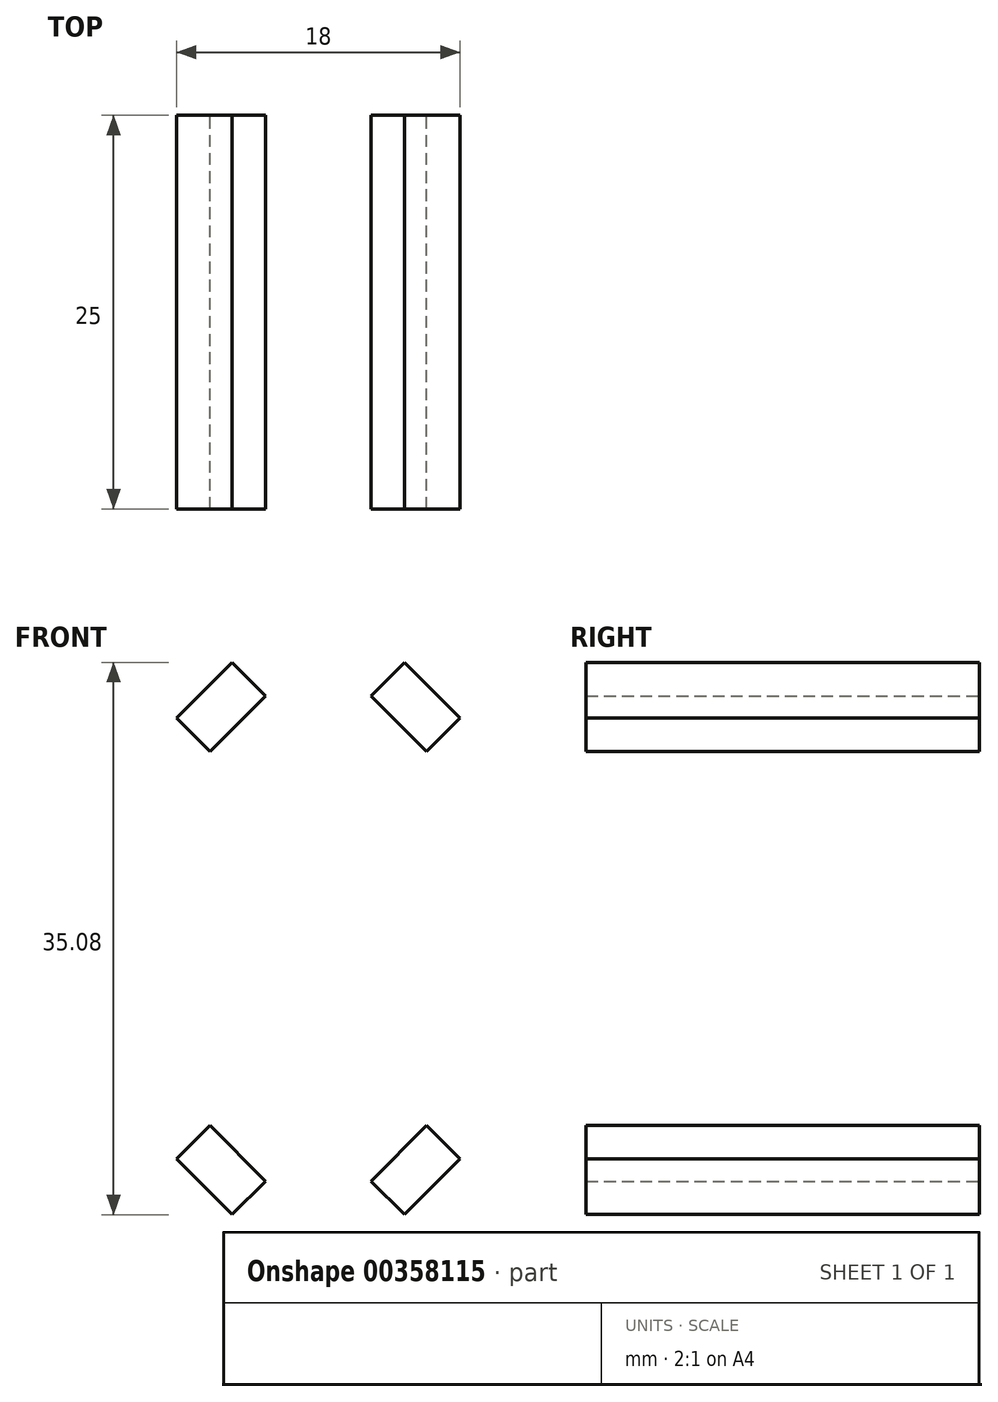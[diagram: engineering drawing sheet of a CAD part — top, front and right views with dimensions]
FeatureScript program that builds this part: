
annotation { "Feature Type Name" : "Feature", "Feature Type Description" : "" }
export const myFeature = defineFeature(function(context is Context, id is Id, definition is map)
    precondition{}
    {
        {
            var Q0;
            Q0=qCreatedBy(makeId("Front.planeOp"),FACE);
            var sketch = newSketch(context, id + "F0", { "sketchPlane" : qUnion([Q0])});
            skPoint(sketch, "E0", {"position": v(-9, -14) * mm});
            skLineSegment(sketch, "E1", {"start": v(-9, -14) * mm, "end": v(-5.46, -17.54) * mm});
            skLineSegment(sketch, "E2", {"start": v(-5.46, -17.54) * mm, "end": v(-3.34, -15.41) * mm});
            skLineSegment(sketch, "E3", {"start": v(-3.34, -15.41) * mm, "end": v(-6.88, -11.88) * mm});
            skLineSegment(sketch, "E4", {"start": v(-6.88, -11.88) * mm, "end": v(-9, -14) * mm});
            skLineSegment(sketch, "E5.MirrorCS", {"start": v(9, -14) * mm, "end": v(5.46, -17.54) * mm});
            skLineSegment(sketch, "E6.MirrorCS", {"start": v(3.34, -15.41) * mm, "end": v(6.88, -11.88) * mm});
            skPoint(sketch, "E7.MirrorP", {"position": v(9, -14) * mm});
            skLineSegment(sketch, "E8.MirrorCS", {"start": v(6.88, -11.88) * mm, "end": v(9, -14) * mm});
            skLineSegment(sketch, "E9.MirrorCS", {"start": v(5.46, -17.54) * mm, "end": v(3.34, -15.41) * mm});
            skLineSegment(sketch, "E10.MirrorCS", {"start": v(5.46, 17.54) * mm, "end": v(3.34, 15.41) * mm});
            skLineSegment(sketch, "E11.MirrorCS", {"start": v(-5.46, 17.54) * mm, "end": v(-3.34, 15.41) * mm});
            skPoint(sketch, "E12.MirrorP", {"position": v(9, 14) * mm});
            skPoint(sketch, "E13.MirrorP", {"position": v(-9, 14) * mm});
            skLineSegment(sketch, "E14.MirrorCS", {"start": v(-6.88, 11.88) * mm, "end": v(-9, 14) * mm});
            skLineSegment(sketch, "E15.MirrorCS", {"start": v(6.88, 11.88) * mm, "end": v(9, 14) * mm});
            skLineSegment(sketch, "E16.MirrorCS", {"start": v(-9, 14) * mm, "end": v(-5.46, 17.54) * mm});
            skLineSegment(sketch, "E17.MirrorCS", {"start": v(-3.34, 15.41) * mm, "end": v(-6.88, 11.88) * mm});
            skLineSegment(sketch, "E18.MirrorCS", {"start": v(9, 14) * mm, "end": v(5.46, 17.54) * mm});
            skLineSegment(sketch, "E19.MirrorCS", {"start": v(3.34, 15.41) * mm, "end": v(6.88, 11.88) * mm});
            skSolve(sketch);
        }
        {
            var Q0;
            Q0=makeQuery(id+"F0.imprint","IMPRINT",FACE,{"disambiguationData":[TD([[makeQuery(id+"F0.imprint","IMPRINT",EDGE,{"derivedFrom":sQuery(id+"F0.wireOp",EDGE,"E1")}),1.0]])]});
            var Q1;
            Q1=makeQuery(id+"F0.imprint","IMPRINT",FACE,{"disambiguationData":[TD([[makeQuery(id+"F0.imprint","IMPRINT",EDGE,{"derivedFrom":sQuery(id+"F0.wireOp",EDGE,"E5.MirrorCS")}),-1.0]])]});
            var Q2;
            Q2=makeQuery(id+"F0.imprint","IMPRINT",FACE,{"disambiguationData":[TD([[makeQuery(id+"F0.imprint","IMPRINT",EDGE,{"derivedFrom":sQuery(id+"F0.wireOp",EDGE,"E10.MirrorCS")}),1.0]])]});
            var Q3;
            Q3=makeQuery(id+"F0.imprint","IMPRINT",FACE,{"disambiguationData":[TD([[makeQuery(id+"F0.imprint","IMPRINT",EDGE,{"derivedFrom":sQuery(id+"F0.wireOp",EDGE,"E11.MirrorCS")}),-1.0]])]});
            extrude(context, id + "F1", {"entities" : qUnion([Q0, Q1, Q2, Q3]), "depth" : 25 * mm});
        }
    });
